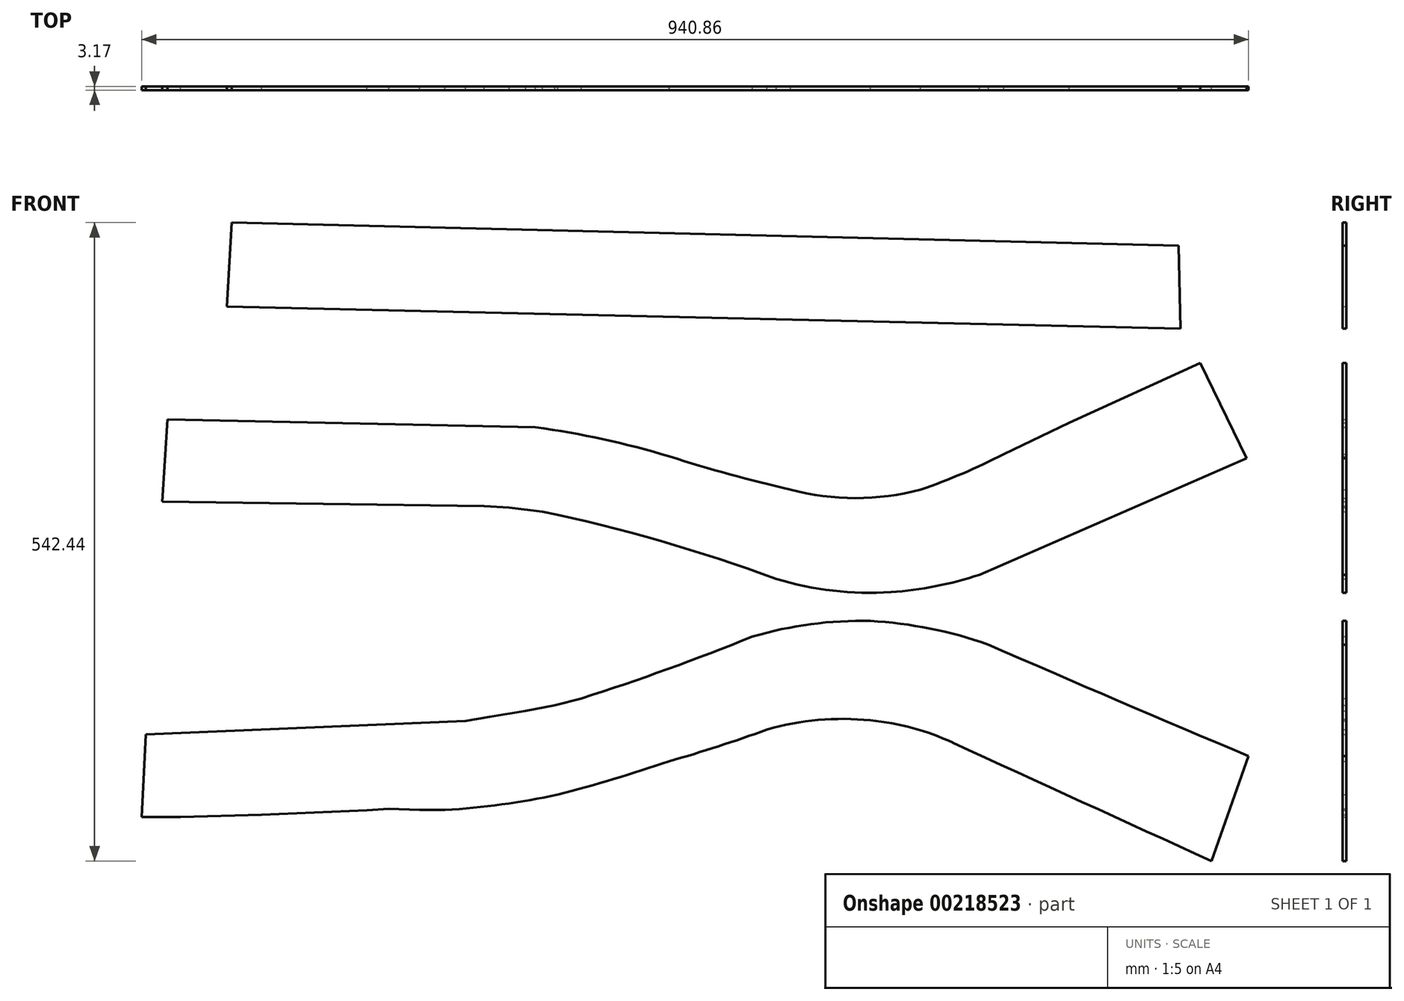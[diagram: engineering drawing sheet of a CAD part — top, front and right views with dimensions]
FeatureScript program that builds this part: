
annotation { "Feature Type Name" : "Feature", "Feature Type Description" : "" }
export const myFeature = defineFeature(function(context is Context, id is Id, definition is map)
    precondition{}
    {
        {
            var Q0;
            Q0=qCreatedBy(makeId("Front.planeOp"),FACE);
            var sketch = newSketch(context, id + "F0", { "sketchPlane" : qUnion([Q0])});
            skLineSegment(sketch, "E0", {"start": v(-9.98, -35.23) * mm, "end": v(-5.75, 34.8) * mm});
            skLineSegment(sketch, "E1", {"start": v(-5.75, 34.8) * mm, "end": v(307.12, 28.15) * mm});
            skLineSegment(sketch, "E2", {"start": v(-9.98, -35.23) * mm, "end": v(263.64, -38.97) * mm});
            skLineSegment(sketch, "E3", {"start": v(263.64, -38.97) * mm, "end": v(284.92, -40.26) * mm});
            skLineSegment(sketch, "E4", {"start": v(284.92, -40.26) * mm, "end": v(312.94, -43.55) * mm});
            skArc(sketch, "E5", {"start": v(421.12, 3.3) * mm, "mid": v(364.61, 17.97) * mm, "end": v(307.12, 28.15) * mm});
            skArc(sketch, "E6", {"start": v(421.12, 3.3) * mm, "mid": v(472.19, -11.87) * mm, "end": v(523.85, -24.87) * mm});
            skArc(sketch, "E7", {"start": v(523.85, -24.87) * mm, "mid": v(579.2, -32.08) * mm, "end": v(634.54, -24.87) * mm});
            skArc(sketch, "E8", {"start": v(634.54, -24.87) * mm, "mid": v(670.4, -11.15) * mm, "end": v(705.06, 5.37) * mm});
            skArc(sketch, "E9", {"start": v(511.78, -100.82) * mm, "mid": v(413.42, -68.52) * mm, "end": v(312.94, -43.55) * mm});
            skArc(sketch, "E10", {"start": v(511.78, -100.82) * mm, "mid": v(560.02, -110.75) * mm, "end": v(609.25, -111.96) * mm});
            skArc(sketch, "E11", {"start": v(609.25, -111.96) * mm, "mid": v(647.3, -106.95) * mm, "end": v(684.42, -97.19) * mm});
            skLineSegment(sketch, "E12", {"start": v(684.42, -97.19) * mm, "end": v(911.42, 1.9) * mm});
            skLineSegment(sketch, "E13", {"start": v(911.42, 1.9) * mm, "end": v(872.21, 82.82) * mm});
            skLineSegment(sketch, "E14", {"start": v(872.21, 82.82) * mm, "end": v(760.76, 31.93) * mm});
            skLineSegment(sketch, "E15", {"start": v(760.76, 31.93) * mm, "end": v(705.06, 5.37) * mm});
            skLineSegment(sketch, "E16", {"start": v(-24.06, -232.92) * mm, "end": v(-27.65, -303) * mm});
            skLineSegment(sketch, "E17", {"start": v(-27.65, -303) * mm, "end": v(5.27, -303) * mm});
            skLineSegment(sketch, "E18", {"start": v(5.27, -303) * mm, "end": v(74.35, -301.25) * mm});
            skLineSegment(sketch, "E19", {"start": v(74.35, -301.25) * mm, "end": v(163.78, -297.23) * mm});
            skLineSegment(sketch, "E20", {"start": v(163.78, -297.23) * mm, "end": v(182.7, -296.07) * mm});
            skLineSegment(sketch, "E21", {"start": v(182.7, -296.07) * mm, "end": v(208.62, -297.1) * mm});
            skLineSegment(sketch, "E22", {"start": v(208.62, -297.1) * mm, "end": v(230.13, -297.1) * mm});
            skLineSegment(sketch, "E23", {"start": v(-24.06, -232.92) * mm, "end": v(247.6, -221.4) * mm});
            skLineSegment(sketch, "E24", {"start": v(247.6, -221.4) * mm, "end": v(268.04, -217.9) * mm});
            skLineSegment(sketch, "E25", {"start": v(268.04, -217.9) * mm, "end": v(298.66, -212.96) * mm});
            skLineSegment(sketch, "E26", {"start": v(298.66, -212.96) * mm, "end": v(323.51, -208.01) * mm});
            skLineSegment(sketch, "E27", {"start": v(323.51, -208.01) * mm, "end": v(346.24, -202.33) * mm});
            skArc(sketch, "E28", {"start": v(346.24, -202.33) * mm, "mid": v(419.43, -177.37) * mm, "end": v(491.66, -149.74) * mm});
            skArc(sketch, "E29", {"start": v(591.85, -136.48) * mm, "mid": v(541.24, -139.21) * mm, "end": v(491.66, -149.74) * mm});
            skArc(sketch, "E30", {"start": v(692.07, -156.57) * mm, "mid": v(642.67, -142.97) * mm, "end": v(591.85, -136.48) * mm});
            skArc(sketch, "E31", {"start": v(230.13, -297.1) * mm, "mid": v(278.38, -292.32) * mm, "end": v(326.15, -284.02) * mm});
            skArc(sketch, "E32", {"start": v(326.15, -284.02) * mm, "mid": v(373.65, -270.75) * mm, "end": v(420.63, -255.77) * mm});
            skArc(sketch, "E33", {"start": v(420.63, -255.77) * mm, "mid": v(462.5, -243) * mm, "end": v(503.9, -228.75) * mm});
            skArc(sketch, "E34", {"start": v(591.85, -220.93) * mm, "mid": v(547.5, -220.62) * mm, "end": v(503.9, -228.75) * mm});
            skArc(sketch, "E35", {"start": v(661.98, -239.95) * mm, "mid": v(627.73, -227.4) * mm, "end": v(591.85, -220.93) * mm});
            skArc(sketch, "E36", {"start": v(692.07, -156.57) * mm, "mid": v(802.46, -204.33) * mm, "end": v(913.2, -251.28) * mm});
            skArc(sketch, "E37", {"start": v(661.98, -239.95) * mm, "mid": v(771.75, -290.3) * mm, "end": v(881.64, -340.4) * mm});
            skLineSegment(sketch, "E38", {"start": v(913.2, -251.28) * mm, "end": v(881.64, -340.4) * mm});
            skLineSegment(sketch, "E39", {"start": v(49.06, 202.05) * mm, "end": v(44.87, 130.6) * mm});
            skLineSegment(sketch, "E40", {"start": v(44.87, 130.6) * mm, "end": v(855.35, 111.84) * mm});
            skLineSegment(sketch, "E41", {"start": v(855.35, 111.84) * mm, "end": v(853.65, 182.28) * mm});
            skLineSegment(sketch, "E42", {"start": v(853.65, 182.28) * mm, "end": v(49.06, 202.05) * mm});
            skSolve(sketch);
        }
        {
            var Q0;
            Q0 = qSketchRegion(id + "F0", true);
            extrude(context, id + "F1", {"entities" : qUnion([Q0]), "depth" : 3.17 * mm});
        }
    });
